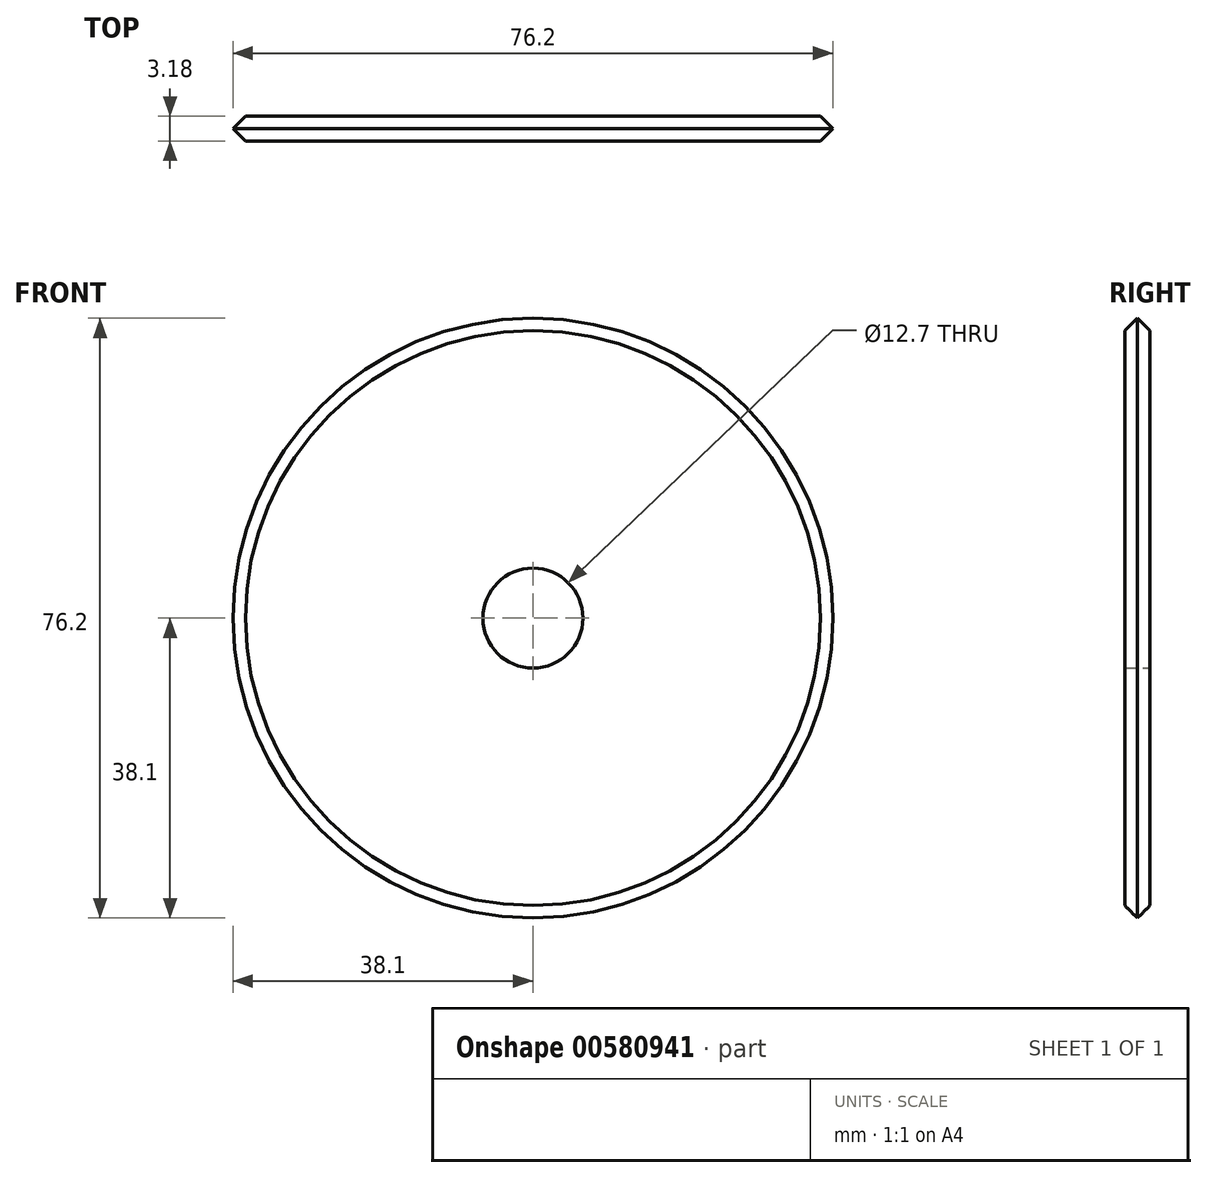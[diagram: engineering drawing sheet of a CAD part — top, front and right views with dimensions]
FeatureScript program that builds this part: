
annotation { "Feature Type Name" : "Feature", "Feature Type Description" : "" }
export const myFeature = defineFeature(function(context is Context, id is Id, definition is map)
    precondition{}
    {
        {
            var Q0;
            Q0=qCreatedBy(makeId("Front.planeOp"),FACE);
            var sketch = newSketch(context, id + "F0", { "sketchPlane" : qUnion([Q0])});
            skCircle(sketch, "E0", {"center": v(0, 0) * mm, "radius": 38.1 * mm});
            skCircle(sketch, "E1", {"center": v(0, 0) * mm, "radius": 6.35 * mm});
            skSolve(sketch);
        }
        {
            var Q0;
            Q0=makeQuery(id+"F0.imprint","IMPRINT",FACE,{"disambiguationData":[TD([[makeQuery(id+"F0.imprint","IMPRINT",EDGE,{"derivedFrom":sQuery(id+"F0.wireOp",EDGE,"E0")}),1.0]])]});
            extrude(context, id + "F1", {"entities" : qUnion([Q0]), "endBound" : BoundingType.SYMMETRIC, "depth" : 3.17 * mm, "offsetDistance" : 25.4 * mm});
        }
        {
            var Q0;
            Q0=makeQuery(id+"F1.opExtrude","CAP_EDGE",EDGE,{"disambiguationData":[OSD([sQuery(id+"F0.wireOp",EDGE,"E0")])],"isStart":true});
            var Q1;
            Q1=makeQuery(id+"F1.opExtrude","CAP_EDGE",EDGE,{"disambiguationData":[OSD([sQuery(id+"F0.wireOp",EDGE,"E0")])],"isStart":false});
            chamfer(context, id + "F2", {"entities" : qUnion([Q0, Q1]), "width" : 1.59 * mm, "tangentPropagation" : true});
        }
    });
